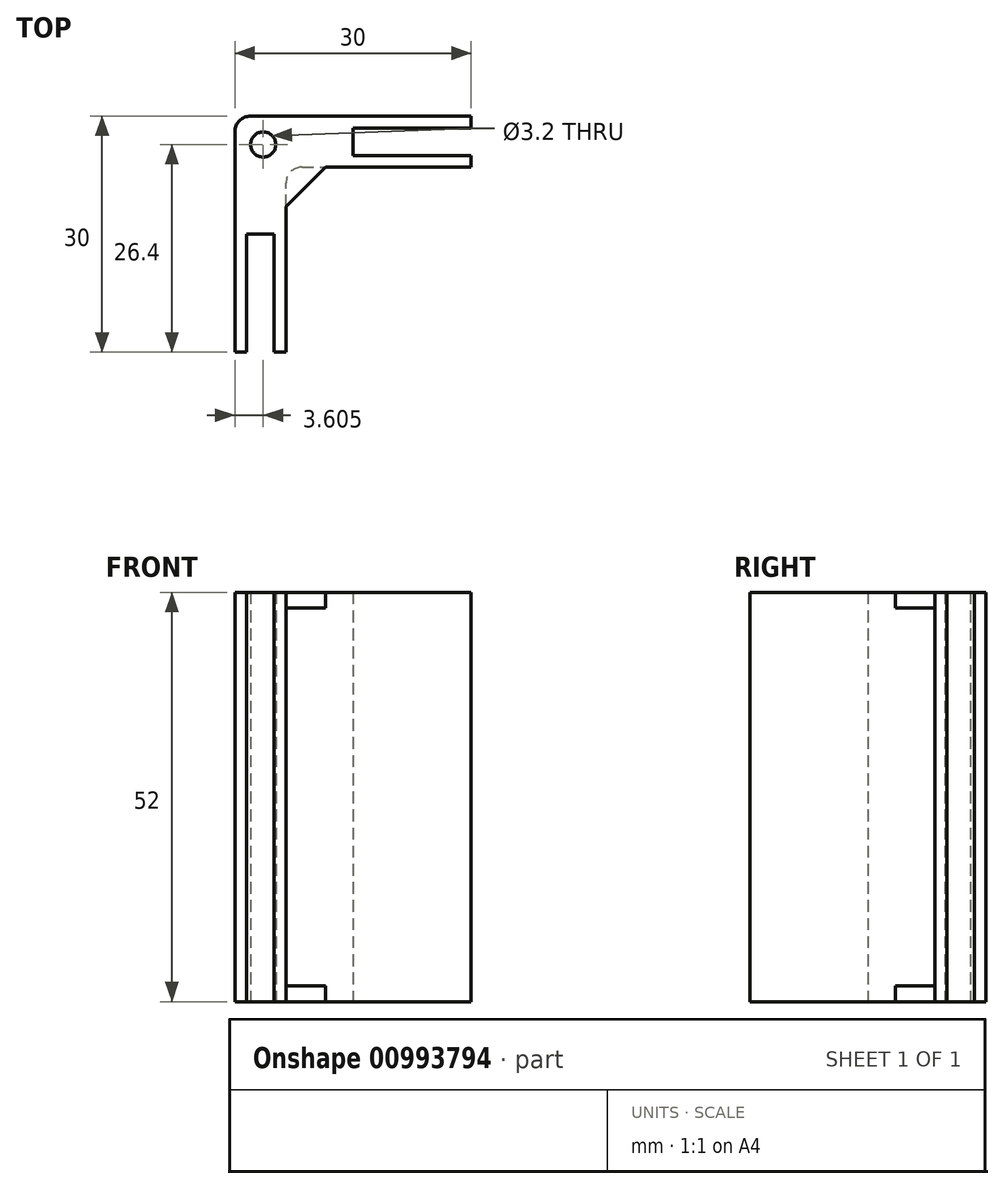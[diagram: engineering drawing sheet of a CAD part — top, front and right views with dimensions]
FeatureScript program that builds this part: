
annotation { "Feature Type Name" : "Feature", "Feature Type Description" : "" }
export const myFeature = defineFeature(function(context is Context, id is Id, definition is map)
    precondition{}
    {
        {
            var Q0;
            Q0=qCreatedBy(makeId("Top.planeOp"),FACE);
            var sketch = newSketch(context, id + "F0", { "sketchPlane" : qUnion([Q0])});
            skLineSegment(sketch, "E0", {"start": v(22.35, 11.5) * mm, "end": v(-7.65, 11.5) * mm});
            skLineSegment(sketch, "E1", {"start": v(-7.65, 11.5) * mm, "end": v(-7.65, -18.5) * mm});
            skLineSegment(sketch, "E2", {"start": v(-7.65, -18.5) * mm, "end": v(-6.15, -18.5) * mm});
            skLineSegment(sketch, "E3", {"start": v(-6.15, -18.5) * mm, "end": v(-6.15, -3.5) * mm});
            skLineSegment(sketch, "E4", {"start": v(-6.15, -3.5) * mm, "end": v(-2.65, -3.5) * mm});
            skLineSegment(sketch, "E5", {"start": v(-2.65, -3.5) * mm, "end": v(-2.65, -18.5) * mm});
            skLineSegment(sketch, "E6", {"start": v(-2.65, -18.5) * mm, "end": v(-1.15, -18.5) * mm});
            skLineSegment(sketch, "E7", {"start": v(-1.15, -18.5) * mm, "end": v(-1.15, 5) * mm});
            skLineSegment(sketch, "E8", {"start": v(-1.15, 5) * mm, "end": v(22.35, 5) * mm});
            skLineSegment(sketch, "E9", {"start": v(22.35, 5) * mm, "end": v(22.35, 6.5) * mm});
            skLineSegment(sketch, "E10", {"start": v(22.35, 6.5) * mm, "end": v(7.35, 6.5) * mm});
            skLineSegment(sketch, "E11", {"start": v(7.35, 6.5) * mm, "end": v(7.35, 10) * mm});
            skLineSegment(sketch, "E12", {"start": v(7.35, 10) * mm, "end": v(22.35, 10) * mm});
            skLineSegment(sketch, "E13", {"start": v(22.35, 10) * mm, "end": v(22.35, 11.5) * mm});
            skCircle(sketch, "E14", {"center": v(-4.05, 7.9) * mm, "radius": 1.6 * mm});
            skLineSegment(sketch, "E15", {"start": v(-1.15, 0) * mm, "end": v(3.85, 5) * mm});
            skSolve(sketch);
        }
        {
            var Q0;
            Q0=makeQuery(id+"F0.imprint","IMPRINT",FACE,{"disambiguationData":[TD([[makeQuery(id+"F0.imprint","IMPRINT",EDGE,{"derivedFrom":sQuery(id+"F0.wireOp",EDGE,"E0")}),1.0]])]});
            extrude(context, id + "F1", {"entities" : qUnion([Q0]), "depth" : 52 * mm, "offsetDistance" : 25 * mm});
        }
        {
            var Q0;
            {var subQ3=sQuery(id+"F0.wireOp",EDGE,"E15");Q0=makeQuery(id+"F0.imprint","IMPRINT",FACE,{"disambiguationData":[TD([[makeQuery(id+"F0.imprint","IMPRINT",EDGE,{"derivedFrom":subQ3}),1.0]])]});}
            extrude(context, id + "F2", {"entities" : qUnion([Q0]), "operationType" : NewBodyOperationType.ADD, "depth" : 2 * mm, "offsetDistance" : 25 * mm});
        }
        {
            var Q0;
            Q0=makeQuery(id+"F1.opExtrude","CAP_FACE",FACE,{"disambiguationData":[OSD([sQuery(id+"F0.wireOp",EDGE,"E0"),sQuery(id+"F0.wireOp",EDGE,"E1"),sQuery(id+"F0.wireOp",EDGE,"E2"),sQuery(id+"F0.wireOp",EDGE,"E3"),sQuery(id+"F0.wireOp",EDGE,"E4"),sQuery(id+"F0.wireOp",EDGE,"E5"),sQuery(id+"F0.wireOp",EDGE,"E6"),sQuery(id+"F0.wireOp",EDGE,"E7"),sQuery(id+"F0.wireOp",EDGE,"E8"),sQuery(id+"F0.wireOp",EDGE,"E9"),sQuery(id+"F0.wireOp",EDGE,"E10"),sQuery(id+"F0.wireOp",EDGE,"E11"),sQuery(id+"F0.wireOp",EDGE,"E12"),sQuery(id+"F0.wireOp",EDGE,"E13"),sQuery(id+"F0.wireOp",EDGE,"E14")])],"isStart":false});
            var sketch = newSketch(context, id + "F3", { "sketchPlane" : qUnion([Q0])});
            skLineSegment(sketch, "E16", {"start": v(3.85, 5) * mm, "end": v(-1.15, 0) * mm});
            skSolve(sketch);
        }
        {
            var Q0;
            {var subQ0=sQuery(id+"F3.wireOp",EDGE,"E16");Q0=makeQuery(id+"F3.imprint","IMPRINT",FACE,{"disambiguationData":[TD([[makeQuery(id+"F3.imprint","IMPRINT",EDGE,{"derivedFrom":subQ0}),-1.0]])]});}
            extrude(context, id + "F4", {"entities" : qUnion([Q0]), "operationType" : NewBodyOperationType.ADD, "oppositeDirection" : true, "depth" : 2 * mm, "offsetDistance" : 25 * mm});
        }
        {
            var Q0;
            Q0=makeQuery(id+"F1.opExtrude","SWEPT_EDGE",EDGE,{"disambiguationData":[OSD([sQuery(id+"F0.wireOp",EDGE,"E7"),sQuery(id+"F0.wireOp",EDGE,"E8")])]});
            var Q1;
            Q1=makeQuery(id+"F2.opExtrude","SWEPT_EDGE",EDGE,{"disambiguationData":[OSD([sQuery(id+"F0.wireOp",EDGE,"E8"),sQuery(id+"F0.wireOp",EDGE,"E15")])]});
            var Q2;
            Q2=makeQuery(id+"F2.opExtrude","SWEPT_EDGE",EDGE,{"disambiguationData":[OSD([sQuery(id+"F0.wireOp",EDGE,"E7"),sQuery(id+"F0.wireOp",EDGE,"E15")])]});
            var Q3;
            Q3=makeQuery(id+"F4.opExtrude","SWEPT_EDGE",EDGE,{"disambiguationData":[OSD([sQuery(id+"F0.wireOp",EDGE,"E7"),sQuery(id+"F3.wireOp",EDGE,"E16")])]});
            var Q4;
            Q4=makeQuery(id+"F4.opExtrude","SWEPT_EDGE",EDGE,{"disambiguationData":[OSD([sQuery(id+"F0.wireOp",EDGE,"E8"),sQuery(id+"F3.wireOp",EDGE,"E16")])]});
            var Q5;
            Q5=makeQuery(id+"F1.opExtrude","SWEPT_EDGE",EDGE,{"disambiguationData":[OSD([sQuery(id+"F0.wireOp",EDGE,"E0"),sQuery(id+"F0.wireOp",EDGE,"E1")])]});
            fillet(context, id + "F5", {"entities" : qUnion([Q0, Q1, Q2, Q3, Q4, Q5]), "tangentPropagation" : true, "radius" : 2 * mm, "defaultsChanged" : false, "vertexSettings" : [], "allowEdgeOverflow" : false});
        }
    });
